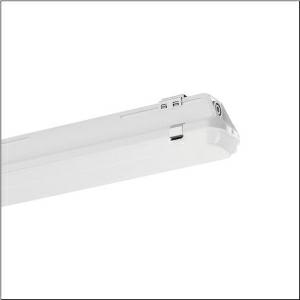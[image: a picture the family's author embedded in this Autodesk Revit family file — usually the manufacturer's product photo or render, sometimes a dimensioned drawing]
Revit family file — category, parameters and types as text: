
# Revit family: monsun_11_51fp20ep460l007
name_source: partatom
category: Lighting Fixtures
units: mm (PartAtom-declared; Revit-internal decimal feet)

## family parameters
Cut with Voids When Loaded = No
Host = Face
Light Source = No
Part Type = Normal
Room Calculation Point = No
Round Connector Dimension = Use Diameter
Shared = No

## types (1)
- --- (1 x LED, 5450 lm, 31.5 W, 4000K)
    Apparent Load = 32 VA
    CIE Flux Codes = 45 75 93 94 100
    Color Rendering = 80
    Color Temperature = 4000K
    Default Elevation = 1800 mm
    Description = Monsun 11, damp-proof luminaire, chain hanger, primary optical cover: enclosure, of PC, light emission: direct distribution, primary light characteristic: symmetric, installation type: suspended mounting, surface-mounted, horizontal mounting, vertical mounting, LED, rated luminous flux: 5.450lm, luminous efficacy: 173lm/W, light colour: 840, colour temperature: 4000K, control gear: DALI 2, with terminal, 5-pole, max. 2.5mm², through-wiring: 7x 2.5mm², mains connection: 220..240V, AC, 50/60Hz, rated input power: 32W, housing, of glass-fibre reinforced polyester, uncoated, bright grey, incl. chain hanger, length: 1.590mm, width: 90mm, height: 88mm, clip for enclosure, of stainless steel (V2A), ceiling mounting element, of stainless steel (V2A), chain hanger, of stainless steel (V2A), protection rating (complete): IP66, insulation class (complete): insulation class I (protective earthing), certification: CE, ENEC, VDE, UKCA, protection symbol: D, impact resistance: IK08, permissible operating ambient temperature: -25..+30°C, standard: EN 50419, EN 60598-2-1, corresponds to IFS (International Featured Standards) requirements for safety and quality in the food industry, for indoor or canopied outdoor use, no direct snow, no direct sun, no direct rain, LABS conformity tested according to VDMA 24364:2018-05, contact your sales advisor before using the luminaires in applications with unclear chemical exposure, large temperature fluctuations or condensation-forming humidity, packaging unit: 1 piece
    Height = 89 mm
    Lamp = 1 x LED
    Lamp Light Flux = 5450 lm
    Lamp Power = 31.5 W
    Lamp count = 1
    Length = 1590 mm
    Luminous efficacy = 173 lm/W
    Manufacturer = Siteco
    ModVariant = No
    Model = 51FP20EP460L007
    Mounting Place = Ceiling
    Mounting Type = Surface mounted
    Number of Poles = 1
    OnlyDefault = Yes
    Power Factor = 1
    Product Name = Monsun 11
    Product group = damp-proof luminaire
    ProductGroupID = 300
    Protection Class = Protection class I
    Protection Degree = IP 66
    RLX_Detail_Level = 1
    RLX_Emergency_Light_Flux = 0 lm
    RLX_Emergency_Type = 0
    RLX_Emergency_Type_DB = No
    RlxData = <blob elided: 92497 chars, md5=0bff7563>
    Socket = socket
    Standby Power = 0 W
    System Light Flux = 5450 lm
    System Power = 32 W
    Type Comments = factory setting: luminous flux: 100 % | dim-lin: 254 | 219 mA
    Type Image = l_1349237.jpg
    URL = http://relux.com
    VarID = @adj_034077
    Voltage = 0 V
    Weight = 0.00 kg
    Width = 90 mm

## geometry (parser evidence)
native form markers: Blend x4, Sweep x13
no freeform markers — native parametric forms only
